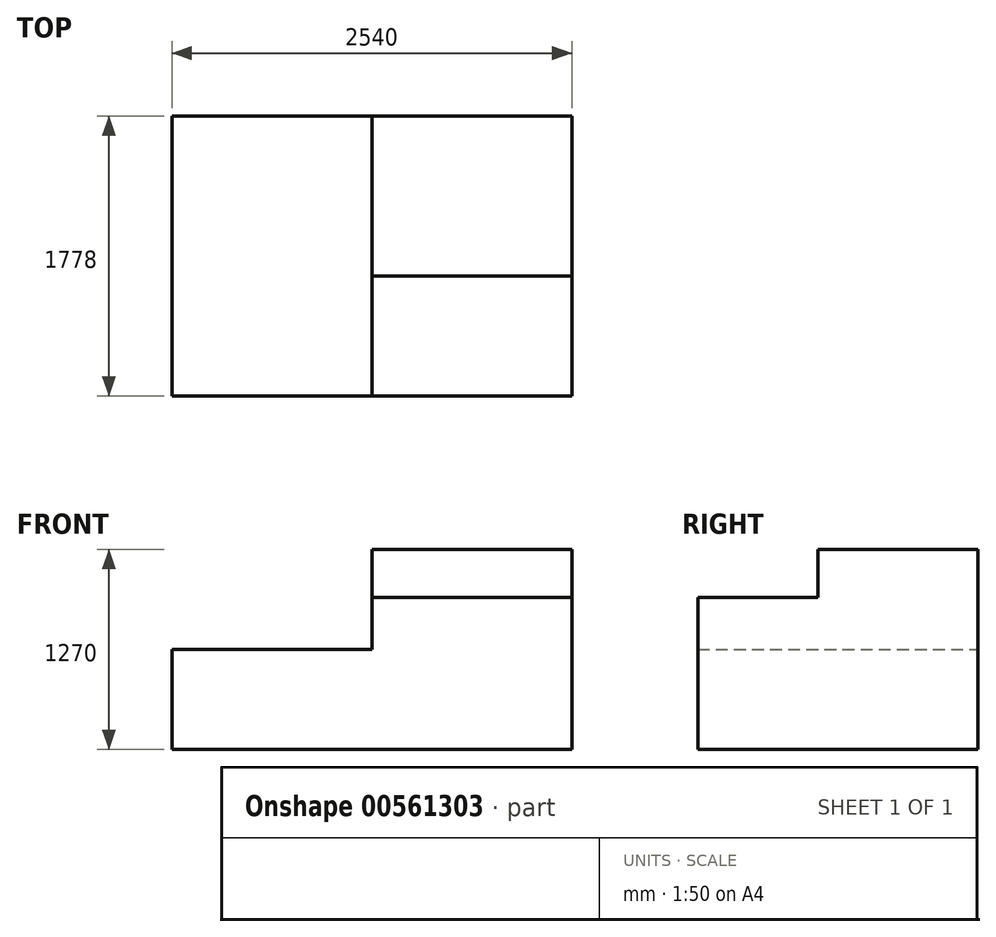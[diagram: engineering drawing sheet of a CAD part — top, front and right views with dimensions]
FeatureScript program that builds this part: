
annotation { "Feature Type Name" : "Feature", "Feature Type Description" : "" }
export const myFeature = defineFeature(function(context is Context, id is Id, definition is map)
    precondition{}
    {
        {
            var Q0;
            Q0=qCreatedBy(makeId("Front.planeOp"),FACE);
            var sketch = newSketch(context, id + "F0", { "sketchPlane" : qUnion([Q0])});
            skLineSegment(sketch, "E0", {"start": v(-74.67, -74.45) * mm, "end": v(2465.33, -74.45) * mm});
            skLineSegment(sketch, "E1", {"start": v(2465.33, -74.45) * mm, "end": v(2465.33, 890.75) * mm});
            skLineSegment(sketch, "E2", {"start": v(2465.33, 890.75) * mm, "end": v(1195.33, 890.75) * mm});
            skLineSegment(sketch, "E3", {"start": v(1195.33, 890.75) * mm, "end": v(1195.33, 560.55) * mm});
            skLineSegment(sketch, "E4", {"start": v(1195.33, 560.55) * mm, "end": v(-74.67, 560.55) * mm});
            skLineSegment(sketch, "E5", {"start": v(-74.67, 560.55) * mm, "end": v(-74.67, -74.45) * mm});
            skLineSegment(sketch, "E6", {"start": v(1195.33, 890.75) * mm, "end": v(1195.33, 1195.55) * mm});
            skLineSegment(sketch, "E7", {"start": v(1195.33, 1195.55) * mm, "end": v(2465.33, 1195.55) * mm});
            skLineSegment(sketch, "E8", {"start": v(2465.33, 1195.55) * mm, "end": v(2465.33, 890.75) * mm});
            skSolve(sketch);
        }
        {
            var Q0;
            Q0=makeQuery(id+"F0.imprint","IMPRINT",FACE,{"disambiguationData":[TD([[makeQuery(id+"F0.imprint","IMPRINT",EDGE,{"derivedFrom":sQuery(id+"F0.wireOp",EDGE,"E0")}),1.0]])]});
            extrude(context, id + "F1", {"entities" : qUnion([Q0]), "depth" : 1778 * mm, "offsetDistance" : 25.4 * mm});
        }
        {
            var Q0;
            Q0=makeQuery(id+"F0.imprint","IMPRINT",FACE,{"disambiguationData":[TD([[makeQuery(id+"F0.imprint","IMPRINT",EDGE,{"derivedFrom":sQuery(id+"F0.wireOp",EDGE,"E2")}),-1.0]])]});
            extrude(context, id + "F2", {"entities" : qUnion([Q0]), "operationType" : NewBodyOperationType.ADD, "depth" : 1016 * mm, "offsetDistance" : 25.4 * mm});
        }
    });
